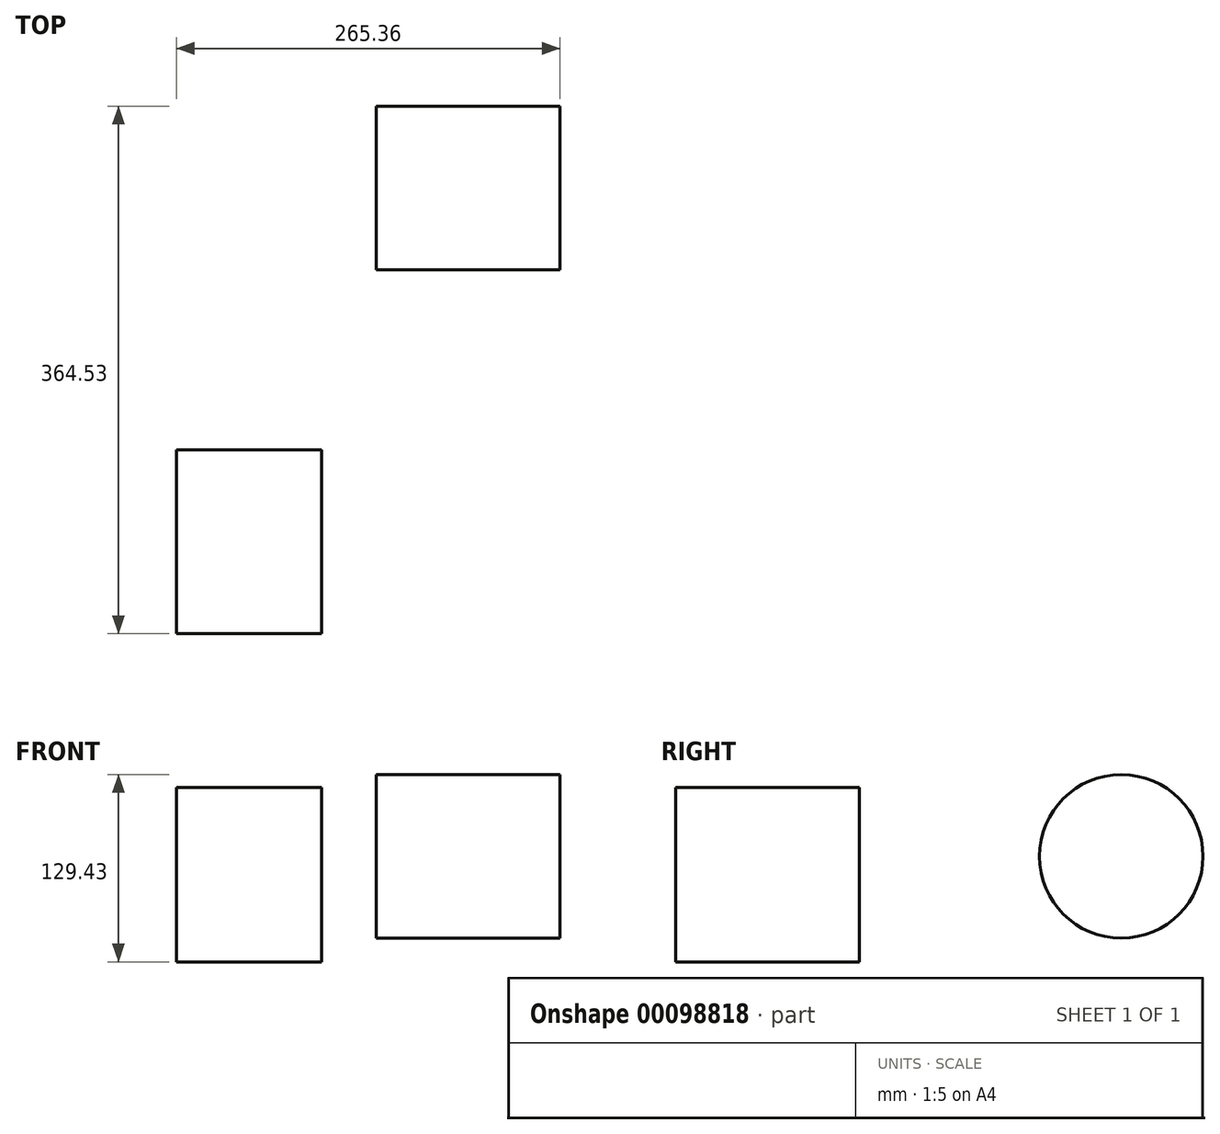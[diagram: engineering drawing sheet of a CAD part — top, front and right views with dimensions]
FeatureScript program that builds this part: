
annotation { "Feature Type Name" : "Feature", "Feature Type Description" : "" }
export const myFeature = defineFeature(function(context is Context, id is Id, definition is map)
    precondition{}
    {
        {
            var Q0;
            Q0=qCreatedBy(makeId("Front.planeOp"),FACE);
            var sketch = newSketch(context, id + "F0", { "sketchPlane" : qUnion([Q0])});
            skLineSegment(sketch, "E0.bottom", {"start": v(-138.36, 53.2) * mm, "end": v(-38, 53.2) * mm});
            skLineSegment(sketch, "E0.top", {"start": v(-138.36, -67.35) * mm, "end": v(-38, -67.35) * mm});
            skLineSegment(sketch, "E0.left", {"start": v(-138.36, 53.2) * mm, "end": v(-138.36, -67.35) * mm});
            skLineSegment(sketch, "E0.right", {"start": v(-38, 53.2) * mm, "end": v(-38, -67.35) * mm});
            skSolve(sketch);
        }
        {
            var Q0;
            Q0=makeQuery(id+"F0.imprint","IMPRINT",FACE,{"disambiguationData":[TD([[makeQuery(id+"F0.imprint","IMPRINT",EDGE,{"derivedFrom":sQuery(id+"F0.wireOp",EDGE,"E0.bottom")}),-1.0]])]});
            extrude(context, id + "F1", {"entities" : qUnion([Q0]), "depth" : 127 * mm});
        }
        {
            var Q0;
            Q0=qCreatedBy(makeId("Right.planeOp"),FACE);
            var sketch = newSketch(context, id + "F2", { "sketchPlane" : qUnion([Q0])});
            skCircle(sketch, "E1", {"center": v(180.99, 5.53) * mm, "radius": 56.54 * mm});
            skSolve(sketch);
        }
        {
            var Q0;
            Q0=makeQuery(id+"F2.imprint","IMPRINT",FACE,{"disambiguationData":[TD([[makeQuery(id+"F2.imprint","IMPRINT",EDGE,{"derivedFrom":sQuery(id+"F2.wireOp",EDGE,"E1")}),1.0]])]});
            extrude(context, id + "F3", {"entities" : qUnion([Q0]), "depth" : 127 * mm});
        }
    });
